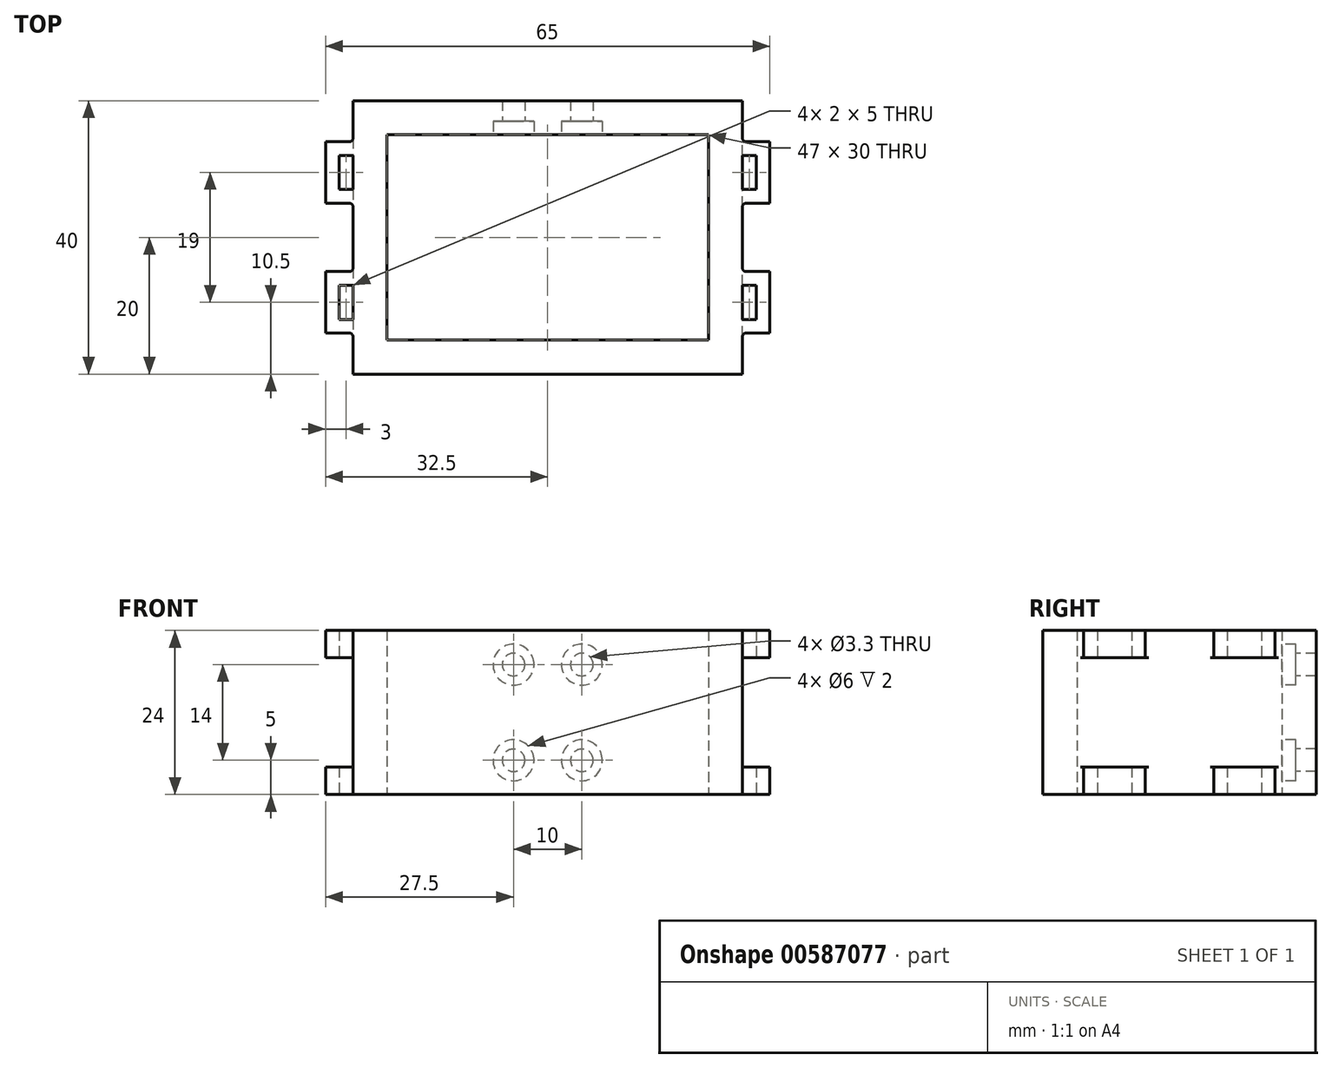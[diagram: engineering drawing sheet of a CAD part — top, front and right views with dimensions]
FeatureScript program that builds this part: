
annotation { "Feature Type Name" : "Feature", "Feature Type Description" : "" }
export const myFeature = defineFeature(function(context is Context, id is Id, definition is map)
    precondition{}
    {
        {
            var Q0;
            Q0=qCreatedBy(makeId("Top.planeOp"),FACE);
            var sketch = newSketch(context, id + "F0", { "sketchPlane" : qUnion([Q0])});
            skLineSegment(sketch, "E0.bottom", {"start": v(23.5, -15) * mm, "end": v(-23.5, -15) * mm});
            skLineSegment(sketch, "E0.top", {"start": v(23.5, 15) * mm, "end": v(-23.5, 15) * mm});
            skLineSegment(sketch, "E0.left", {"start": v(23.5, -15) * mm, "end": v(23.5, 15) * mm});
            skLineSegment(sketch, "E0.right", {"start": v(-23.5, -15) * mm, "end": v(-23.5, 15) * mm});
            skPoint(sketch, "E0.middle", {"position": v(0, 0) * mm});
            skLineSegment(sketch, "E1.0", {"start": v(28.5, 20) * mm, "end": v(-28.5, 20) * mm});
            skLineSegment(sketch, "E1.1", {"start": v(28.5, -20) * mm, "end": v(28.5, -14.5) * mm});
            skLineSegment(sketch, "E1.2", {"start": v(28.5, -20) * mm, "end": v(-28.5, -20) * mm});
            skLineSegment(sketch, "E1.3", {"start": v(-28.5, -20) * mm, "end": v(-28.5, -14.5) * mm});
            skLineSegment(sketch, "E2", {"start": v(0, 27.26) * mm, "end": v(0, -32.82) * mm, "construction": true});
            skLineSegment(sketch, "E3.bottom", {"start": v(-28.5, 12) * mm, "end": v(-30.5, 12) * mm});
            skLineSegment(sketch, "E3.top", {"start": v(-28.5, 7) * mm, "end": v(-30.5, 7) * mm});
            skLineSegment(sketch, "E3.left", {"start": v(-28.5, 12) * mm, "end": v(-28.5, 7) * mm});
            skLineSegment(sketch, "E3.right", {"start": v(-30.5, 12) * mm, "end": v(-30.5, 7) * mm});
            skLineSegment(sketch, "E4.bottom", {"start": v(-28.5, -7) * mm, "end": v(-30.5, -7) * mm});
            skLineSegment(sketch, "E4.top", {"start": v(-28.5, -12) * mm, "end": v(-30.5, -12) * mm});
            skLineSegment(sketch, "E4.left", {"start": v(-28.5, -7) * mm, "end": v(-28.5, -12) * mm});
            skLineSegment(sketch, "E4.right", {"start": v(-30.5, -7) * mm, "end": v(-30.5, -12) * mm});
            skLineSegment(sketch, "E5.bottom", {"start": v(-29, 14) * mm, "end": v(-32.5, 14) * mm});
            skLineSegment(sketch, "E5.top", {"start": v(-29, 5) * mm, "end": v(-32.5, 5) * mm});
            skLineSegment(sketch, "E5.right", {"start": v(-32.5, 14) * mm, "end": v(-32.5, 5) * mm});
            skLineSegment(sketch, "E6.bottom", {"start": v(-29, -14) * mm, "end": v(-32.5, -14) * mm});
            skLineSegment(sketch, "E6.top", {"start": v(-29, -5) * mm, "end": v(-32.5, -5) * mm});
            skLineSegment(sketch, "E6.right", {"start": v(-32.5, -14) * mm, "end": v(-32.5, -5) * mm});
            skLineSegment(sketch, "E7.MirrorCS", {"start": v(28.5, -7) * mm, "end": v(30.5, -7) * mm});
            skLineSegment(sketch, "E8.MirrorCS", {"start": v(28.5, -12) * mm, "end": v(30.5, -12) * mm});
            skLineSegment(sketch, "E9.MirrorCS", {"start": v(28.5, 7) * mm, "end": v(30.5, 7) * mm});
            skLineSegment(sketch, "E10.MirrorCS", {"start": v(28.5, 12) * mm, "end": v(30.5, 12) * mm});
            skLineSegment(sketch, "E11.MirrorCS", {"start": v(28.5, 12) * mm, "end": v(28.5, 7) * mm});
            skLineSegment(sketch, "E12.MirrorCS", {"start": v(28.5, -7) * mm, "end": v(28.5, -12) * mm});
            skLineSegment(sketch, "E13.MirrorCS", {"start": v(30.5, -7) * mm, "end": v(30.5, -12) * mm});
            skLineSegment(sketch, "E14.MirrorCS", {"start": v(29, 5) * mm, "end": v(32.5, 5) * mm});
            skLineSegment(sketch, "E15.MirrorCS", {"start": v(32.5, 14) * mm, "end": v(32.5, 5) * mm});
            skLineSegment(sketch, "E16.MirrorCS", {"start": v(29, -5) * mm, "end": v(32.5, -5) * mm});
            skLineSegment(sketch, "E17.MirrorCS", {"start": v(28.5, -12) * mm, "end": v(28.5, -7) * mm});
            skLineSegment(sketch, "E18.MirrorCS", {"start": v(30.5, 12) * mm, "end": v(30.5, 7) * mm});
            skLineSegment(sketch, "E19.MirrorCS", {"start": v(32.5, -14) * mm, "end": v(32.5, -5) * mm});
            skLineSegment(sketch, "E20.MirrorCS", {"start": v(29, -14) * mm, "end": v(32.5, -14) * mm});
            skLineSegment(sketch, "E21.MirrorCS", {"start": v(29, 14) * mm, "end": v(32.5, 14) * mm});
            skLineSegment(sketch, "E22.trimOffspring", {"start": v(-28.5, 14.5) * mm, "end": v(-28.5, 20) * mm});
            skLineSegment(sketch, "E23.trimOffspring", {"start": v(-28.5, 7) * mm, "end": v(-28.5, 12) * mm});
            skLineSegment(sketch, "E24.trimOffspring", {"start": v(-28.5, -4.5) * mm, "end": v(-28.5, 4.5) * mm});
            skLineSegment(sketch, "E25.trimOffspring", {"start": v(-28.5, -12) * mm, "end": v(-28.5, -7) * mm});
            skLineSegment(sketch, "E26.trimOffspring", {"start": v(28.5, -4.5) * mm, "end": v(28.5, 4.5) * mm});
            skLineSegment(sketch, "E27.trimOffspring", {"start": v(28.5, 14.5) * mm, "end": v(28.5, 20) * mm});
            skLineSegment(sketch, "E28.trimOffspring", {"start": v(28.5, 7) * mm, "end": v(28.5, 12) * mm});
            skPoint(sketch, "E29.visualSharp", {"position": v(-28.5, 14) * mm});
            skArc(sketch, "E29.filletArc", {"start": v(-29, 14) * mm, "mid": v(-28.65, 14.15) * mm, "end": v(-28.5, 14.5) * mm});
            skPoint(sketch, "E30.visualSharp", {"position": v(-28.5, 5) * mm});
            skArc(sketch, "E30.filletArc", {"start": v(-28.5, 4.5) * mm, "mid": v(-28.65, 4.85) * mm, "end": v(-29, 5) * mm});
            skPoint(sketch, "E31.visualSharp", {"position": v(-28.5, -5) * mm});
            skArc(sketch, "E31.filletArc", {"start": v(-29, -5) * mm, "mid": v(-28.65, -4.85) * mm, "end": v(-28.5, -4.5) * mm});
            skPoint(sketch, "E32.visualSharp", {"position": v(-28.5, -14) * mm});
            skArc(sketch, "E32.filletArc", {"start": v(-28.5, -14.5) * mm, "mid": v(-28.65, -14.15) * mm, "end": v(-29, -14) * mm});
            skPoint(sketch, "E33.visualSharp", {"position": v(28.5, 14) * mm});
            skArc(sketch, "E33.filletArc", {"start": v(28.5, 14.5) * mm, "mid": v(28.65, 14.15) * mm, "end": v(29, 14) * mm});
            skPoint(sketch, "E34.visualSharp", {"position": v(28.5, 5) * mm});
            skArc(sketch, "E34.filletArc", {"start": v(29, 5) * mm, "mid": v(28.65, 4.85) * mm, "end": v(28.5, 4.5) * mm});
            skPoint(sketch, "E35.visualSharp", {"position": v(28.5, -5) * mm});
            skArc(sketch, "E35.filletArc", {"start": v(28.5, -4.5) * mm, "mid": v(28.65, -4.85) * mm, "end": v(29, -5) * mm});
            skPoint(sketch, "E36.visualSharp", {"position": v(28.5, -14) * mm});
            skArc(sketch, "E36.filletArc", {"start": v(29, -14) * mm, "mid": v(28.65, -14.15) * mm, "end": v(28.5, -14.5) * mm});
            skSolve(sketch);
        }
        {
            var Q0;
            Q0 = qSketchRegion(id + "F0", true);
            extrude(context, id + "F1", {"entities" : qUnion([Q0]), "depth" : 24 * mm, "offsetDistance" : 25 * mm});
        }
        {
            var Q0;
            Q0=makeQuery(id+"F1.opExtrude","SWEPT_FACE",FACE,{"disambiguationData":[OSD([sQuery(id+"F0.wireOp",EDGE,"E15.MirrorCS")])]});
            var sketch = newSketch(context, id + "F2", { "sketchPlane" : qUnion([Q0])});
            skLineSegment(sketch, "E37.bottom", {"start": v(-20, 20) * mm, "end": v(20, 20) * mm});
            skLineSegment(sketch, "E37.top", {"start": v(-20, 4) * mm, "end": v(20, 4) * mm});
            skLineSegment(sketch, "E37.left", {"start": v(-20, 20) * mm, "end": v(-20, 4) * mm});
            skLineSegment(sketch, "E37.right", {"start": v(20, 20) * mm, "end": v(20, 4) * mm});
            skSolve(sketch);
        }
        {
            var Q0;
            Q0 = qSketchRegion(id + "F2", true);
            extrude(context, id + "F3", {"entities" : qUnion([Q0]), "operationType" : NewBodyOperationType.REMOVE, "oppositeDirection" : true, "depth" : 4 * mm, "offsetDistance" : 25 * mm});
        }
        {
            var Q0;
            Q0=makeQuery(id+"F1.opExtrude","SWEPT_FACE",FACE,{"disambiguationData":[OSD([sQuery(id+"F0.wireOp",EDGE,"E5.right")])]});
            var sketch = newSketch(context, id + "F4", { "sketchPlane" : qUnion([Q0])});
            skLineSegment(sketch, "E38.bottom", {"start": v(-20, 20) * mm, "end": v(20, 20) * mm});
            skLineSegment(sketch, "E38.top", {"start": v(-20, 4) * mm, "end": v(20, 4) * mm});
            skLineSegment(sketch, "E38.left", {"start": v(-20, 20) * mm, "end": v(-20, 4) * mm});
            skLineSegment(sketch, "E38.right", {"start": v(20, 20) * mm, "end": v(20, 4) * mm});
            skSolve(sketch);
        }
        {
            var Q0;
            Q0 = qSketchRegion(id + "F4", true);
            extrude(context, id + "F5", {"entities" : qUnion([Q0]), "operationType" : NewBodyOperationType.REMOVE, "oppositeDirection" : true, "depth" : 4 * mm, "offsetDistance" : 25 * mm});
        }
        {
            var Q0;
            Q0=makeQuery(id+"F1.opExtrude","SWEPT_FACE",FACE,{"disambiguationData":[OSD([sQuery(id+"F0.wireOp",EDGE,"E0.top")])]});
            var sketch = newSketch(context, id + "F6", { "sketchPlane" : qUnion([Q0])});
            skLineSegment(sketch, "E39", {"start": v(0, 38.85) * mm, "end": v(0, -18.85) * mm, "construction": true});
            skPoint(sketch, "E39.startSnap0", {"position": v(0, 24) * mm});
            skPoint(sketch, "E39.endSnap0", {"position": v(0, 24) * mm});
            skCircle(sketch, "E40", {"center": v(-5, 19) * mm, "radius": 1.65 * mm});
            skCircle(sketch, "E41", {"center": v(-5, 5) * mm, "radius": 1.65 * mm});
            skCircle(sketch, "E42.MirrorC", {"center": v(5, 19) * mm, "radius": 1.65 * mm});
            skCircle(sketch, "E43.MirrorC", {"center": v(5, 5) * mm, "radius": 1.65 * mm});
            skSolve(sketch);
        }
        {
            var Q0;
            Q0 = qSketchRegion(id + "F6", true);
            extrude(context, id + "F7", {"entities" : qUnion([Q0]), "operationType" : NewBodyOperationType.REMOVE, "oppositeDirection" : true, "depth" : 25 * mm, "offsetDistance" : 25 * mm});
        }
        {
            var Q0;
            Q0=makeQuery(id+"F1.opExtrude","SWEPT_FACE",FACE,{"disambiguationData":[OSD([sQuery(id+"F0.wireOp",EDGE,"E0.top")])]});
            var sketch = newSketch(context, id + "F8", { "sketchPlane" : qUnion([Q0])});
            skCircle(sketch, "E44", {"center": v(-5, 19) * mm, "radius": 3 * mm});
            skLineSegment(sketch, "E45", {"start": v(0, 15.14) * mm, "end": v(0, -12.7) * mm, "construction": true});
            skCircle(sketch, "E46", {"center": v(-5, 5) * mm, "radius": 3 * mm});
            skCircle(sketch, "E47.MirrorC", {"center": v(5, 19) * mm, "radius": 3 * mm});
            skCircle(sketch, "E48.MirrorC", {"center": v(5, 5) * mm, "radius": 3 * mm});
            skSolve(sketch);
        }
        {
            var Q0;
            Q0 = qSketchRegion(id + "F8", true);
            extrude(context, id + "F9", {"entities" : qUnion([Q0]), "operationType" : NewBodyOperationType.REMOVE, "oppositeDirection" : true, "depth" : 2 * mm, "offsetDistance" : 25 * mm});
        }
    });
